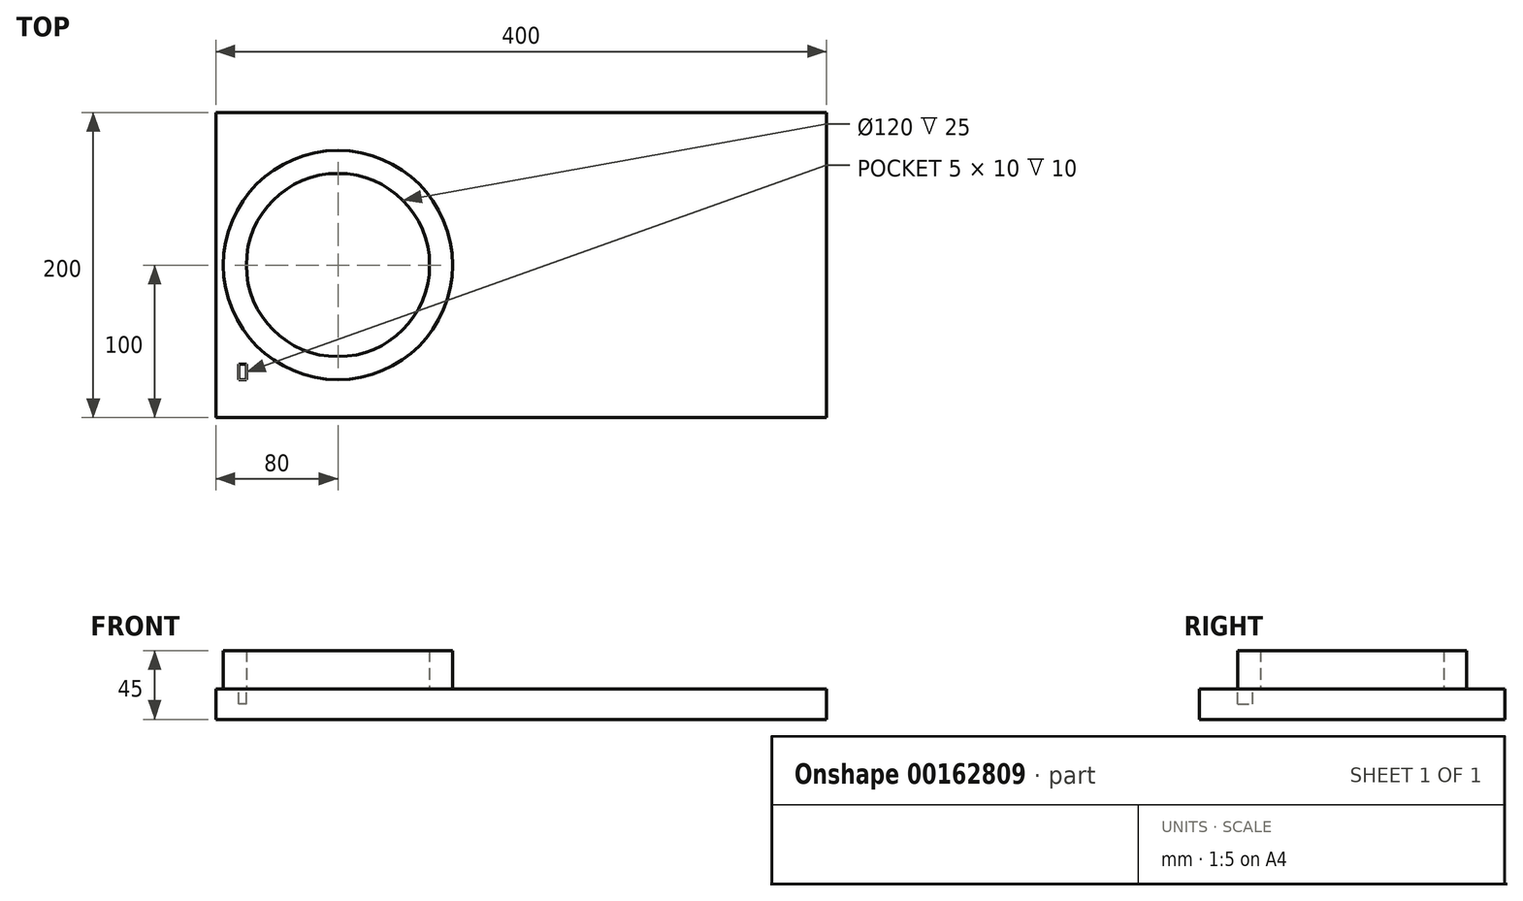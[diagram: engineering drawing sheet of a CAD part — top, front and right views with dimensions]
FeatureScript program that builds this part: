
annotation { "Feature Type Name" : "Feature", "Feature Type Description" : "" }
export const myFeature = defineFeature(function(context is Context, id is Id, definition is map)
    precondition{}
    {
        {
            var Q0;
            Q0=qCreatedBy(makeId("Top.planeOp"),FACE);
            var sketch = newSketch(context, id + "F0", { "sketchPlane" : qUnion([Q0])});
            skLineSegment(sketch, "E0.bottom", {"start": v(-200, 100) * mm, "end": v(200, 100) * mm});
            skLineSegment(sketch, "E0.top", {"start": v(-200, -100) * mm, "end": v(200, -100) * mm});
            skLineSegment(sketch, "E0.left", {"start": v(-200, 100) * mm, "end": v(-200, -100) * mm});
            skLineSegment(sketch, "E0.right", {"start": v(200, 100) * mm, "end": v(200, -100) * mm});
            skPoint(sketch, "E0.middle", {"position": v(0, 0) * mm});
            skSolve(sketch);
        }
        {
            var Q0;
            Q0 = qSketchRegion(id + "F0", true);
            extrude(context, id + "F1", {"entities" : qUnion([Q0]), "depth" : 20 * mm});
        }
        {
            var Q0;
            Q0=makeQuery(id+"F1.opExtrude","CAP_FACE",FACE,{"disambiguationData":[OSD([sQuery(id+"F0.wireOp",EDGE,"E0.bottom"),sQuery(id+"F0.wireOp",EDGE,"E0.top"),sQuery(id+"F0.wireOp",EDGE,"E0.left"),sQuery(id+"F0.wireOp",EDGE,"E0.right")])],"isStart":false});
            var sketch = newSketch(context, id + "F2", { "sketchPlane" : qUnion([Q0])});
            skCircle(sketch, "E1", {"center": v(-120, 0) * mm, "radius": 75 * mm});
            skCircle(sketch, "E2", {"center": v(-120, 0) * mm, "radius": 60 * mm});
            skSolve(sketch);
        }
        {
            var Q0;
            Q0 = qSketchRegion(id + "F2", true);
            extrude(context, id + "F3", {"entities" : qUnion([Q0]), "operationType" : NewBodyOperationType.ADD, "depth" : 25 * mm});
        }
        {
            var Q0;
            {var subQ0=sQuery(id+"F0.wireOp",EDGE,"E0.right");var subQ1=sQuery(id+"F0.wireOp",EDGE,"E0.left");var subQ2=sQuery(id+"F0.wireOp",EDGE,"E0.top");var subQ3=sQuery(id+"F0.wireOp",EDGE,"E0.bottom");Q0=makeQuery(id+"F3.boolean.opBoolean","SPLIT",FACE,{"disambiguationData":[TD([makeQuery(id+"F1.opExtrude","SWEPT_FACE",FACE,{"disambiguationData":[OSD([subQ3])]})])],"derivedFrom":makeQuery(id+"F1.opExtrude","CAP_FACE",FACE,{"disambiguationData":[OSD([subQ3,subQ2,subQ1,subQ0])],"isStart":false})});}
            var sketch = newSketch(context, id + "F4", { "sketchPlane" : qUnion([Q0])});
            skLineSegment(sketch, "E3.bottom", {"start": v(-180, -75) * mm, "end": v(-185, -75) * mm});
            skLineSegment(sketch, "E3.top", {"start": v(-180, -65) * mm, "end": v(-185, -65) * mm});
            skLineSegment(sketch, "E3.left", {"start": v(-180, -75) * mm, "end": v(-180, -65) * mm});
            skLineSegment(sketch, "E3.right", {"start": v(-185, -75) * mm, "end": v(-185, -65) * mm});
            skPoint(sketch, "E3.middle", {"position": v(-182.5, -70) * mm});
            skSolve(sketch);
        }
        {
            var Q0;
            Q0 = qSketchRegion(id + "F4", true);
            extrude(context, id + "F5", {"entities" : qUnion([Q0]), "operationType" : NewBodyOperationType.REMOVE, "oppositeDirection" : true, "depth" : 10 * mm});
        }
    });
